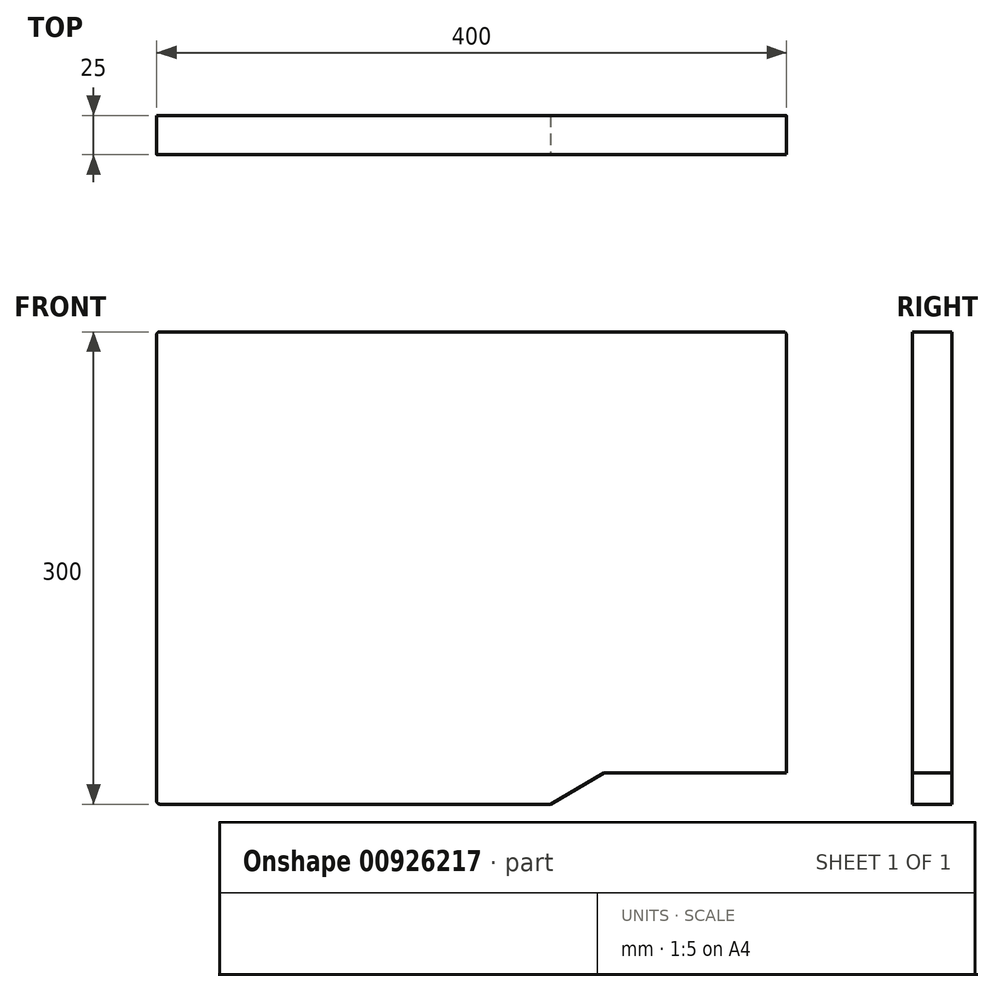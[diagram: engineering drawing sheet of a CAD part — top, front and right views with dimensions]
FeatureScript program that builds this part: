
annotation { "Feature Type Name" : "Feature", "Feature Type Description" : "" }
export const myFeature = defineFeature(function(context is Context, id is Id, definition is map)
    precondition{}
    {
        {
            var Q0;
            Q0=qCreatedBy(makeId("Front.planeOp"),FACE);
            var sketch = newSketch(context, id + "F0", { "sketchPlane" : qUnion([Q0])});
            skLineSegment(sketch, "E0.bottom", {"start": v(-200, -150) * mm, "end": v(200, -150) * mm});
            skLineSegment(sketch, "E0.top", {"start": v(-200, 150) * mm, "end": v(200, 150) * mm});
            skLineSegment(sketch, "E0.left", {"start": v(-200, -150) * mm, "end": v(-200, 150) * mm});
            skLineSegment(sketch, "E0.right", {"start": v(200, -150) * mm, "end": v(200, 150) * mm});
            skLineSegment(sketch, "E1", {"start": v(0, 225.33) * mm, "end": v(0, -169.93) * mm, "construction": true});
            skLineSegment(sketch, "E2", {"start": v(-266.65, 0) * mm, "end": v(309.84, 0) * mm, "construction": true});
            skSolve(sketch);
        }
        {
            var Q0;
            Q0 = qSketchRegion(id + "F0", true);
            extrude(context, id + "F1", {"entities" : qUnion([Q0]), "depth" : 25 * mm, "offsetDistance" : 25 * mm});
        }
        {
            var Q0;
            Q0=makeQuery(id+"F1.opExtrude","CAP_FACE",FACE,{"disambiguationData":[OSD([sQuery(id+"F0.wireOp",EDGE,"E0.bottom"),sQuery(id+"F0.wireOp",EDGE,"E0.top"),sQuery(id+"F0.wireOp",EDGE,"E0.left"),sQuery(id+"F0.wireOp",EDGE,"E0.right")])],"isStart":false});
            var sketch = newSketch(context, id + "F2", { "sketchPlane" : qUnion([Q0])});
            skLineSegment(sketch, "E3.bottom", {"start": v(50, -150) * mm, "end": v(200, -150) * mm});
            skLineSegment(sketch, "E3.top", {"start": v(84.64, -130) * mm, "end": v(200, -130) * mm});
            skLineSegment(sketch, "E3.right", {"start": v(200, -150) * mm, "end": v(200, -130) * mm});
            skLineSegment(sketch, "E4.left", {"start": v(200, -118.6) * mm, "end": v(200, -118.22) * mm});
            skLineSegment(sketch, "E5", {"start": v(50, -150) * mm, "end": v(84.64, -130) * mm});
            skSolve(sketch);
        }
        {
            var Q0;
            Q0 = qSketchRegion(id + "F2", true);
            extrude(context, id + "F3", {"entities" : qUnion([Q0]), "operationType" : NewBodyOperationType.REMOVE, "endBound" : BoundingType.THROUGH_ALL, "oppositeDirection" : true, "depth" : 25 * mm, "offsetDistance" : 25 * mm});
        }
        {
            var Q0;
            Q0=makeQuery(id+"F1.opExtrude","SWEPT_EDGE",EDGE,{"disambiguationData":[OSD([sQuery(id+"F0.wireOp",EDGE,"E0.top"),sQuery(id+"F0.wireOp",EDGE,"E0.right")])]});
            var Q1;
            Q1=makeQuery(id+"F1.opExtrude","SWEPT_EDGE",EDGE,{"disambiguationData":[OSD([sQuery(id+"F0.wireOp",EDGE,"E0.bottom"),sQuery(id+"F0.wireOp",EDGE,"E0.right")])]});
            var Q2;
            Q2=makeQuery(id+"F1.opExtrude","SWEPT_EDGE",EDGE,{"disambiguationData":[OSD([sQuery(id+"F0.wireOp",EDGE,"E0.bottom"),sQuery(id+"F0.wireOp",EDGE,"E0.left")])]});
            var Q3;
            Q3=makeQuery(id+"F1.opExtrude","SWEPT_EDGE",EDGE,{"disambiguationData":[OSD([sQuery(id+"F0.wireOp",EDGE,"E0.top"),sQuery(id+"F0.wireOp",EDGE,"E0.left")])]});
            var Q4;
            Q4=makeQuery(id+"F3.boolean.opBoolean","COPY",EDGE,{"derivedFrom":makeQuery(id+"F3.opExtrude","SWEPT_EDGE",EDGE,{"disambiguationData":[OSD([sQuery(id+"F0.wireOp",EDGE,"E0.bottom"),sQuery(id+"F2.wireOp",EDGE,"E3.bottom"),sQuery(id+"F2.wireOp",EDGE,"E5")])]})});
            var Q5;
            Q5=makeQuery(id+"F3.boolean.opBoolean","COPY",EDGE,{"derivedFrom":makeQuery(id+"F3.opExtrude","SWEPT_EDGE",EDGE,{"disambiguationData":[OSD([sQuery(id+"F2.wireOp",EDGE,"E3.top"),sQuery(id+"F2.wireOp",EDGE,"E5")])]})});
            var Q6;
            Q6=makeQuery(id+"F3.boolean.opBoolean","COPY",EDGE,{"derivedFrom":makeQuery(id+"F3.opExtrude","SWEPT_EDGE",EDGE,{"disambiguationData":[OSD([sQuery(id+"F0.wireOp",EDGE,"E0.right"),sQuery(id+"F2.wireOp",EDGE,"E3.top"),sQuery(id+"F2.wireOp",EDGE,"E3.right")])]})});
            fillet(context, id + "F4", {"entities" : qUnion([Q0, Q1, Q2, Q3, Q4, Q5, Q6]), "radius" : 2 * mm, "tangentPropagation" : true, "allowEdgeOverflow" : false});
        }
    });
